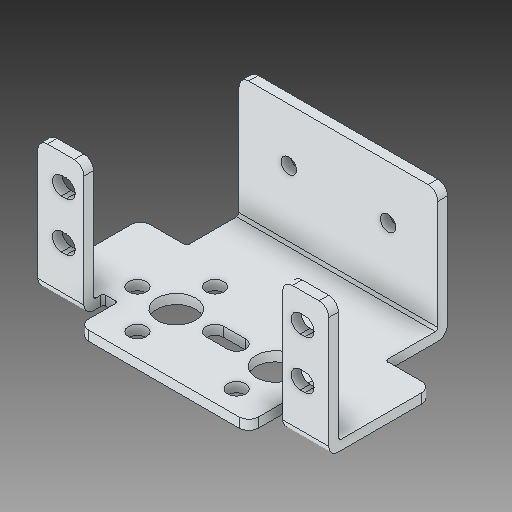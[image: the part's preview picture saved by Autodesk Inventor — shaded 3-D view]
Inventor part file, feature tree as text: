
AUTODESK INVENTOR PART (.ipt)
format: ipt  version: 2019 (Build 230136000, 136)  size: 202,240 bytes
history: native  units: in
note: dims shown in document units (in); Inventor stores cm internally (conversion verified against a paired STEP export)
features: fillet x1
ambient origin geometry x8: Origin, YZ Plane, XZ Plane, XY Plane, X Axis, Y Axis, Z Axis, Center Point
bodies: Solid1 (feature_tree)
feature tree (1):
  fillet  "Fillet16"  [1 undecoded]
note: 1 required parameter value undecoded (feature->parameter linkage not recoverable at this tier; creation-order binding heuristic only, values carry confidence <= 0.55)
